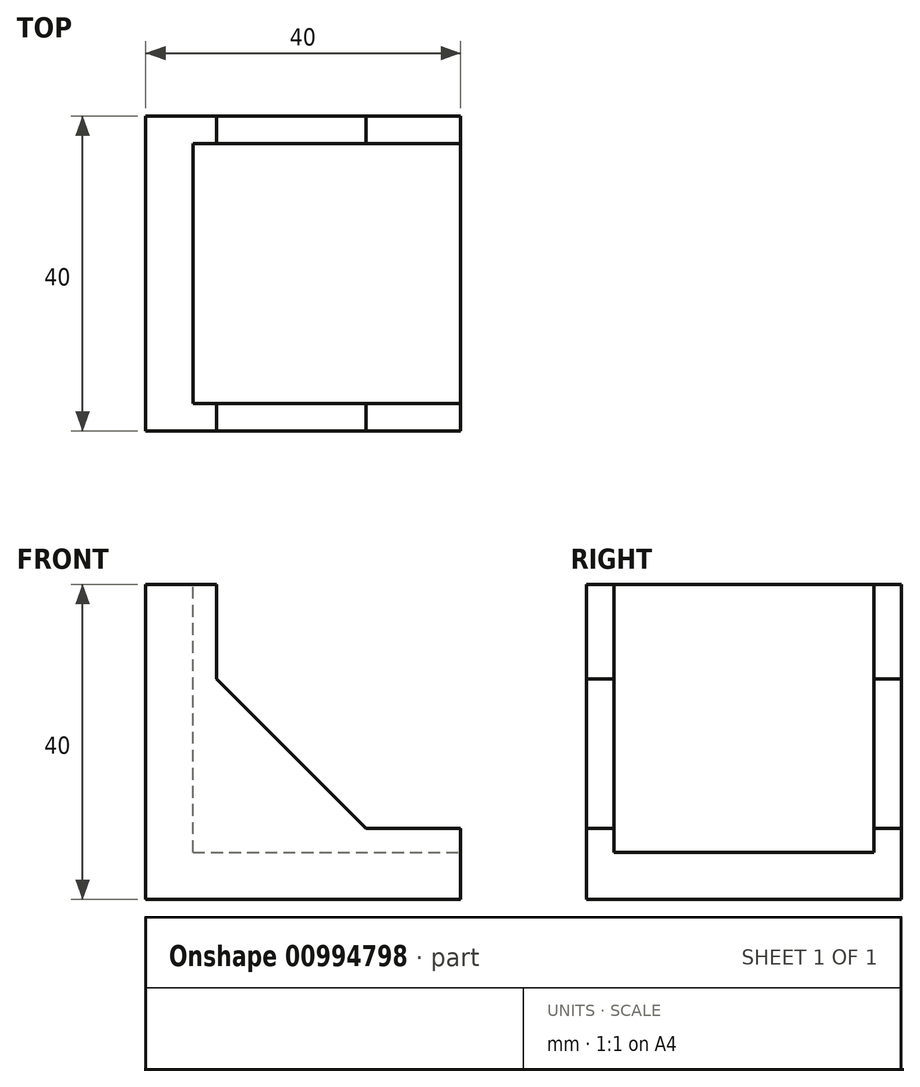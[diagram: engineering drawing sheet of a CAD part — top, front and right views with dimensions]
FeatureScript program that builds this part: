
annotation { "Feature Type Name" : "Feature", "Feature Type Description" : "" }
export const myFeature = defineFeature(function(context is Context, id is Id, definition is map)
    precondition{}
    {
        {
            var Q0;
            Q0=qCreatedBy(makeId("Front.planeOp"),FACE);
            var sketch = newSketch(context, id + "F0", { "sketchPlane" : qUnion([Q0])});
            skLineSegment(sketch, "E0", {"start": v(-20, 20) * mm, "end": v(-20, -20) * mm});
            skLineSegment(sketch, "E1", {"start": v(-20, -20) * mm, "end": v(20, -20) * mm});
            skLineSegment(sketch, "E2", {"start": v(20, -20) * mm, "end": v(20, -14) * mm});
            skLineSegment(sketch, "E3", {"start": v(20, -14) * mm, "end": v(20, -11) * mm});
            skLineSegment(sketch, "E4", {"start": v(20, -11) * mm, "end": v(8, -11) * mm});
            skLineSegment(sketch, "E5", {"start": v(-20, 20) * mm, "end": v(-14, 20) * mm});
            skLineSegment(sketch, "E6", {"start": v(-14, 20) * mm, "end": v(-11, 20) * mm});
            skLineSegment(sketch, "E7", {"start": v(-11, 20) * mm, "end": v(-11, 8) * mm});
            skLineSegment(sketch, "E8", {"start": v(-11, 8) * mm, "end": v(8, -11) * mm});
            skSolve(sketch);
        }
        {
            var Q0;
            Q0 = qSketchRegion(id + "F0", true);
            extrude(context, id + "F1", {"entities" : qUnion([Q0]), "oppositeDirection" : true, "depth" : 40 * mm, "offsetDistance" : 25 * mm});
        }
        {
            var Q0;
            Q0=makeQuery(id+"F1.opExtrude","SWEPT_FACE",FACE,{"disambiguationData":[OSD([sQuery(id+"F0.wireOp",EDGE,"E2"),sQuery(id+"F0.wireOp",EDGE,"E3")])]});
            var sketch = newSketch(context, id + "F2", { "sketchPlane" : qUnion([Q0])});
            skLineSegment(sketch, "E9", {"start": v(36.5, -14) * mm, "end": v(3.5, -14) * mm});
            skLineSegment(sketch, "E10", {"start": v(3.5, -14) * mm, "end": v(3.5, 20) * mm});
            skLineSegment(sketch, "E11", {"start": v(3.5, 20) * mm, "end": v(36.5, 20) * mm});
            skLineSegment(sketch, "E12", {"start": v(36.5, 20) * mm, "end": v(36.5, -14) * mm});
            skSolve(sketch);
        }
        {
            var Q0;
            Q0 = qSketchRegion(id + "F2", true);
            extrude(context, id + "F3", {"entities" : qUnion([Q0]), "operationType" : NewBodyOperationType.REMOVE, "oppositeDirection" : true, "depth" : 34 * mm, "offsetDistance" : 25 * mm});
        }
    });
